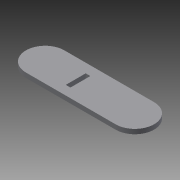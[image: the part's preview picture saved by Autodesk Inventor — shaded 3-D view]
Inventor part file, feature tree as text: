
AUTODESK INVENTOR PART (.ipt)
format: ipt  version: 2013 (Build 170138000, 138)  size: 99,840 bytes
history: native  units: mm
features: other x2, extrude x1, sketch x1
ambient origin geometry x8: Origin, YZ Plane, XZ Plane, XY Plane, X Axis, Y Axis, Z Axis, Center Point
feature tree (4):
  other  "Blocks"
  extrude  "Extrusion5"  Depth=3.0mm
  sketch  "Sketch1"  dims[d0=3.0mm d2=3.0mm d3=0.1mm d7=22.5mm d8=12.4mm d9=4.5mm d10=4.5mm d11=2.0mm d12=2.0mm d23=90.0mm d24=27.0mm d29=3.25mm d30=14.0mm d31=35.0mm d36=13.0mm d38=13.0mm d42=3.25mm d43=0.0mm]
  other  "Block1"
